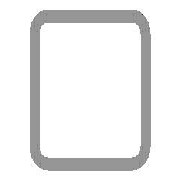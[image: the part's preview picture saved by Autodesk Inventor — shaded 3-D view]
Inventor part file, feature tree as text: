
AUTODESK INVENTOR PART (.ipt)
format: ipt  version: 2018 (Build 220112000, 112)  size: 151,040 bytes
history: native  units: mm (DEFAULTED — no unit token found)
features: sketch x4, other x3, extrude x2, plane x1
ambient origin geometry x8: Origin, YZ Plane, XZ Plane, XY Plane, X Axis, Y Axis, Z Axis, Center Point
bodies: Solid1 (feature_tree)
feature tree (10):
  other  "Driven Length"
  other  "Piano iniziale"
  other  "Piano finale"
  extrude  "Corpo"  TaperAngle=0.0deg  [1 undecoded]
  extrude  "Estrusione2"  Depth=20.0mm
  sketch  "Schizzo"
  sketch  "Sketch3"  dims[d3=300.0mm d4=0.0mm]
  plane  "Work Plane3"
  sketch  "Sketch4"  dims[d7=4.0mm d9=20.0mm d11=20.0mm d12=2.0mm d13=-0.0mm d14=300.0mm d15=10.0mm d16=10.0mm d17=90.0deg d18=300.0mm d19=45.0deg d20=45.0deg d21=10.0mm d22=0.0mm]
  sketch  "Schizzo5"
note: 1 required parameter value undecoded (feature->parameter linkage not recoverable at this tier; creation-order binding heuristic only, values carry confidence <= 0.55)
